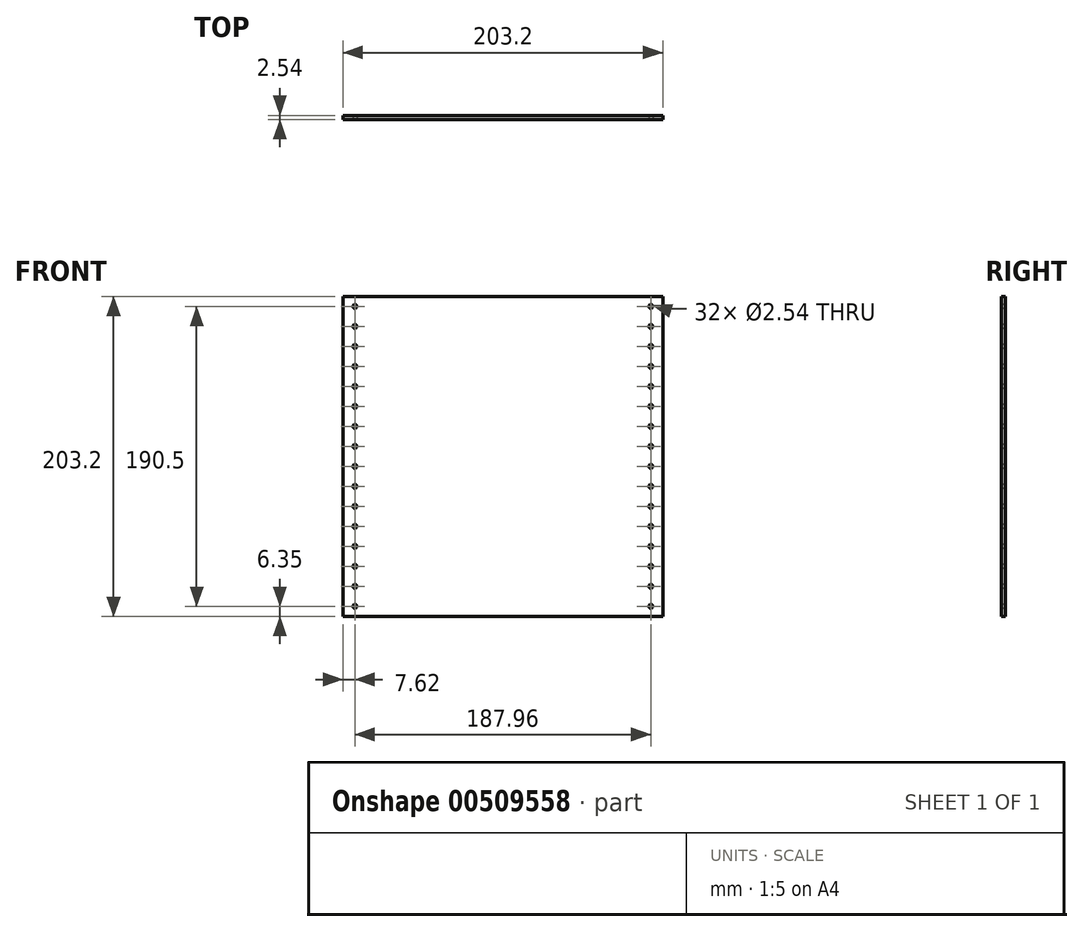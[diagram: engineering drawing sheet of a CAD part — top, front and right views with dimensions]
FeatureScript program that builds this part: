
annotation { "Feature Type Name" : "Feature", "Feature Type Description" : "" }
export const myFeature = defineFeature(function(context is Context, id is Id, definition is map)
    precondition{}
    {
        {
            var Q0;
            Q0=qCreatedBy(makeId("Front.planeOp"),FACE);
            var sketch = newSketch(context, id + "F0", { "sketchPlane" : qUnion([Q0])});
            skLineSegment(sketch, "E0.bottom", {"start": v(0, 0) * mm, "end": v(-203.2, 0) * mm});
            skLineSegment(sketch, "E0.top", {"start": v(0, 203.2) * mm, "end": v(-203.2, 203.2) * mm});
            skLineSegment(sketch, "E0.left", {"start": v(0, 0) * mm, "end": v(0, 203.2) * mm});
            skLineSegment(sketch, "E0.right", {"start": v(-203.2, 0) * mm, "end": v(-203.2, 203.2) * mm});
            skSolve(sketch);
        }
        {
            var Q0;
            Q0=makeQuery(id+"F0.imprint","IMPRINT",FACE,{"disambiguationData":[TD([[makeQuery(id+"F0.imprint","IMPRINT",EDGE,{"derivedFrom":sQuery(id+"F0.wireOp",EDGE,"E0.bottom")}),-1.0]])]});
            extrude(context, id + "F1", {"entities" : qUnion([Q0]), "depth" : 2.54 * mm});
        }
        {
            var Q0;
            Q0=makeQuery(id+"F1.opExtrude","CAP_FACE",FACE,{"disambiguationData":[OSD([sQuery(id+"F0.wireOp",EDGE,"E0.bottom"),sQuery(id+"F0.wireOp",EDGE,"E0.top"),sQuery(id+"F0.wireOp",EDGE,"E0.left"),sQuery(id+"F0.wireOp",EDGE,"E0.right")])],"isStart":false});
            var sketch = newSketch(context, id + "F2", { "sketchPlane" : qUnion([Q0])});
            skLineSegment(sketch, "E1", {"start": v(-203.2, 0) * mm, "end": v(-195.58, 0) * mm});
            skLineSegment(sketch, "E2", {"start": v(-195.58, 0) * mm, "end": v(-195.58, 6.35) * mm});
            skCircle(sketch, "E3", {"center": v(-195.58, 6.35) * mm, "radius": 1.27 * mm});
            skCircle(sketch, "E4.0.1.0", {"center": v(-195.58, 19.05) * mm, "radius": 1.27 * mm});
            skCircle(sketch, "E4.0.2.0", {"center": v(-195.58, 31.75) * mm, "radius": 1.27 * mm});
            skCircle(sketch, "E4.0.3.0", {"center": v(-195.58, 44.45) * mm, "radius": 1.27 * mm});
            skCircle(sketch, "E4.0.4.0", {"center": v(-195.58, 57.15) * mm, "radius": 1.27 * mm});
            skCircle(sketch, "E4.0.5.0", {"center": v(-195.58, 69.85) * mm, "radius": 1.27 * mm});
            skCircle(sketch, "E4.0.6.0", {"center": v(-195.58, 82.55) * mm, "radius": 1.27 * mm});
            skCircle(sketch, "E4.0.7.0", {"center": v(-195.58, 95.25) * mm, "radius": 1.27 * mm});
            skCircle(sketch, "E4.0.8.0", {"center": v(-195.58, 107.95) * mm, "radius": 1.27 * mm});
            skCircle(sketch, "E4.0.9.0", {"center": v(-195.58, 120.65) * mm, "radius": 1.27 * mm});
            skCircle(sketch, "E4.0.10.0", {"center": v(-195.58, 133.35) * mm, "radius": 1.27 * mm});
            skCircle(sketch, "E4.0.11.0", {"center": v(-195.58, 146.05) * mm, "radius": 1.27 * mm});
            skCircle(sketch, "E4.0.12.0", {"center": v(-195.58, 158.75) * mm, "radius": 1.27 * mm});
            skCircle(sketch, "E4.0.13.0", {"center": v(-195.58, 171.45) * mm, "radius": 1.27 * mm});
            skCircle(sketch, "E4.0.14.0", {"center": v(-195.58, 184.15) * mm, "radius": 1.27 * mm});
            skCircle(sketch, "E4.0.15.0", {"center": v(-195.58, 196.85) * mm, "radius": 1.27 * mm});
            skLineSegment(sketch, "E4.direction1", {"start": v(-195.58, 6.35) * mm, "end": v(-170.18, 6.35) * mm, "construction": true});
            skLineSegment(sketch, "E4.direction2", {"start": v(-195.58, 6.35) * mm, "end": v(-195.58, 19.05) * mm, "construction": true});
            skSolve(sketch);
        }
        {
            var Q0;
            Q0=makeQuery(id+"F2.imprint","IMPRINT",FACE,{"disambiguationData":[TD([[makeQuery(id+"F2.imprint","IMPRINT",EDGE,{"derivedFrom":sQuery(id+"F2.wireOp",EDGE,"E4.0.2.0")}),1.0]])]});
            var Q1;
            Q1=makeQuery(id+"F2.imprint","IMPRINT",FACE,{"disambiguationData":[TD([[makeQuery(id+"F2.imprint","IMPRINT",EDGE,{"derivedFrom":sQuery(id+"F2.wireOp",EDGE,"E4.0.3.0")}),1.0]])]});
            var Q2;
            Q2=makeQuery(id+"F2.imprint","IMPRINT",FACE,{"disambiguationData":[TD([[makeQuery(id+"F2.imprint","IMPRINT",EDGE,{"derivedFrom":sQuery(id+"F2.wireOp",EDGE,"E4.0.4.0")}),1.0]])]});
            var Q3;
            Q3=makeQuery(id+"F2.imprint","IMPRINT",FACE,{"disambiguationData":[TD([[makeQuery(id+"F2.imprint","IMPRINT",EDGE,{"derivedFrom":sQuery(id+"F2.wireOp",EDGE,"E4.0.5.0")}),1.0]])]});
            var Q4;
            Q4=makeQuery(id+"F2.imprint","IMPRINT",FACE,{"disambiguationData":[TD([[makeQuery(id+"F2.imprint","IMPRINT",EDGE,{"derivedFrom":sQuery(id+"F2.wireOp",EDGE,"E4.0.6.0")}),1.0]])]});
            var Q5;
            Q5=makeQuery(id+"F2.imprint","IMPRINT",FACE,{"disambiguationData":[TD([[makeQuery(id+"F2.imprint","IMPRINT",EDGE,{"derivedFrom":sQuery(id+"F2.wireOp",EDGE,"E4.0.7.0")}),1.0]])]});
            var Q6;
            Q6=makeQuery(id+"F2.imprint","IMPRINT",FACE,{"disambiguationData":[TD([[makeQuery(id+"F2.imprint","IMPRINT",EDGE,{"derivedFrom":sQuery(id+"F2.wireOp",EDGE,"E4.0.8.0")}),1.0]])]});
            var Q7;
            Q7=makeQuery(id+"F2.imprint","IMPRINT",FACE,{"disambiguationData":[TD([[makeQuery(id+"F2.imprint","IMPRINT",EDGE,{"derivedFrom":sQuery(id+"F2.wireOp",EDGE,"E4.0.9.0")}),1.0]])]});
            var Q8;
            Q8=makeQuery(id+"F2.imprint","IMPRINT",FACE,{"disambiguationData":[TD([[makeQuery(id+"F2.imprint","IMPRINT",EDGE,{"derivedFrom":sQuery(id+"F2.wireOp",EDGE,"E4.0.10.0")}),1.0]])]});
            var Q9;
            Q9=makeQuery(id+"F2.imprint","IMPRINT",FACE,{"disambiguationData":[TD([[makeQuery(id+"F2.imprint","IMPRINT",EDGE,{"derivedFrom":sQuery(id+"F2.wireOp",EDGE,"E4.0.11.0")}),1.0]])]});
            var Q10;
            Q10=makeQuery(id+"F2.imprint","IMPRINT",FACE,{"disambiguationData":[TD([[makeQuery(id+"F2.imprint","IMPRINT",EDGE,{"derivedFrom":sQuery(id+"F2.wireOp",EDGE,"E4.0.12.0")}),1.0]])]});
            var Q11;
            Q11=makeQuery(id+"F2.imprint","IMPRINT",FACE,{"disambiguationData":[TD([[makeQuery(id+"F2.imprint","IMPRINT",EDGE,{"derivedFrom":sQuery(id+"F2.wireOp",EDGE,"E4.0.15.0")}),1.0]])]});
            var Q12;
            Q12=makeQuery(id+"F2.imprint","IMPRINT",FACE,{"disambiguationData":[TD([[makeQuery(id+"F2.imprint","IMPRINT",EDGE,{"derivedFrom":sQuery(id+"F2.wireOp",EDGE,"E4.0.13.0")}),1.0]])]});
            var Q13;
            Q13=makeQuery(id+"F2.imprint","IMPRINT",FACE,{"disambiguationData":[TD([[makeQuery(id+"F2.imprint","IMPRINT",EDGE,{"derivedFrom":sQuery(id+"F2.wireOp",EDGE,"E4.0.14.0")}),1.0]])]});
            var Q14;
            Q14=makeQuery(id+"F2.imprint","IMPRINT",FACE,{"disambiguationData":[TD([[makeQuery(id+"F2.imprint","IMPRINT",EDGE,{"derivedFrom":sQuery(id+"F2.wireOp",EDGE,"E4.0.1.0")}),1.0]])]});
            var Q15;
            Q15=makeQuery(id+"F2.imprint","IMPRINT",FACE,{"disambiguationData":[TD([[makeQuery(id+"F2.imprint","IMPRINT",EDGE,{"derivedFrom":sQuery(id+"F2.wireOp",EDGE,"E3")}),1.0]])]});
            extrude(context, id + "F3", {"entities" : qUnion([Q0, Q1, Q2, Q3, Q4, Q5, Q6, Q7, Q8, Q9, Q10, Q11, Q12, Q13, Q14, Q15]), "operationType" : NewBodyOperationType.REMOVE, "oppositeDirection" : true, "depth" : 25.4 * mm});
        }
        {
            var Q0;
            Q0=makeQuery(id+"F1.opExtrude","CAP_FACE",FACE,{"disambiguationData":[OSD([sQuery(id+"F0.wireOp",EDGE,"E0.bottom"),sQuery(id+"F0.wireOp",EDGE,"E0.top"),sQuery(id+"F0.wireOp",EDGE,"E0.left"),sQuery(id+"F0.wireOp",EDGE,"E0.right")])],"isStart":false});
            var sketch = newSketch(context, id + "F4", { "sketchPlane" : qUnion([Q0])});
            skLineSegment(sketch, "E5", {"start": v(0, 0) * mm, "end": v(-7.62, 0) * mm});
            skLineSegment(sketch, "E6", {"start": v(-7.62, 0) * mm, "end": v(-7.62, 6.35) * mm});
            skCircle(sketch, "E7", {"center": v(-7.62, 6.35) * mm, "radius": 1.27 * mm});
            skCircle(sketch, "E8.0.1.0", {"center": v(-7.62, 19.05) * mm, "radius": 1.27 * mm});
            skCircle(sketch, "E8.0.2.0", {"center": v(-7.62, 31.75) * mm, "radius": 1.27 * mm});
            skCircle(sketch, "E8.0.3.0", {"center": v(-7.62, 44.45) * mm, "radius": 1.27 * mm});
            skCircle(sketch, "E8.0.4.0", {"center": v(-7.62, 57.15) * mm, "radius": 1.27 * mm});
            skCircle(sketch, "E8.0.5.0", {"center": v(-7.62, 69.85) * mm, "radius": 1.27 * mm});
            skCircle(sketch, "E8.0.6.0", {"center": v(-7.62, 82.55) * mm, "radius": 1.27 * mm});
            skCircle(sketch, "E8.0.7.0", {"center": v(-7.62, 95.25) * mm, "radius": 1.27 * mm});
            skCircle(sketch, "E8.0.8.0", {"center": v(-7.62, 107.95) * mm, "radius": 1.27 * mm});
            skCircle(sketch, "E8.0.9.0", {"center": v(-7.62, 120.65) * mm, "radius": 1.27 * mm});
            skCircle(sketch, "E8.0.10.0", {"center": v(-7.62, 133.35) * mm, "radius": 1.27 * mm});
            skCircle(sketch, "E8.0.11.0", {"center": v(-7.62, 146.05) * mm, "radius": 1.27 * mm});
            skCircle(sketch, "E8.0.12.0", {"center": v(-7.62, 158.75) * mm, "radius": 1.27 * mm});
            skCircle(sketch, "E8.0.13.0", {"center": v(-7.62, 171.45) * mm, "radius": 1.27 * mm});
            skCircle(sketch, "E8.0.14.0", {"center": v(-7.62, 184.15) * mm, "radius": 1.27 * mm});
            skCircle(sketch, "E8.0.15.0", {"center": v(-7.62, 196.85) * mm, "radius": 1.27 * mm});
            skLineSegment(sketch, "E8.direction1", {"start": v(-7.62, 6.35) * mm, "end": v(17.78, 6.35) * mm, "construction": true});
            skLineSegment(sketch, "E8.direction2", {"start": v(-7.62, 6.35) * mm, "end": v(-7.62, 19.05) * mm, "construction": true});
            skSolve(sketch);
        }
        {
            var Q0;
            Q0=makeQuery(id+"F4.imprint","IMPRINT",FACE,{"disambiguationData":[TD([[makeQuery(id+"F4.imprint","IMPRINT",EDGE,{"derivedFrom":sQuery(id+"F4.wireOp",EDGE,"E8.0.3.0")}),1.0]])]});
            var Q1;
            Q1=makeQuery(id+"F4.imprint","IMPRINT",FACE,{"disambiguationData":[TD([[makeQuery(id+"F4.imprint","IMPRINT",EDGE,{"derivedFrom":sQuery(id+"F4.wireOp",EDGE,"E8.0.4.0")}),1.0]])]});
            var Q2;
            Q2=makeQuery(id+"F4.imprint","IMPRINT",FACE,{"disambiguationData":[TD([[makeQuery(id+"F4.imprint","IMPRINT",EDGE,{"derivedFrom":sQuery(id+"F4.wireOp",EDGE,"E8.0.5.0")}),1.0]])]});
            var Q3;
            Q3=makeQuery(id+"F4.imprint","IMPRINT",FACE,{"disambiguationData":[TD([[makeQuery(id+"F4.imprint","IMPRINT",EDGE,{"derivedFrom":sQuery(id+"F4.wireOp",EDGE,"E8.0.6.0")}),1.0]])]});
            var Q4;
            Q4=makeQuery(id+"F4.imprint","IMPRINT",FACE,{"disambiguationData":[TD([[makeQuery(id+"F4.imprint","IMPRINT",EDGE,{"derivedFrom":sQuery(id+"F4.wireOp",EDGE,"E8.0.7.0")}),1.0]])]});
            var Q5;
            Q5=makeQuery(id+"F4.imprint","IMPRINT",FACE,{"disambiguationData":[TD([[makeQuery(id+"F4.imprint","IMPRINT",EDGE,{"derivedFrom":sQuery(id+"F4.wireOp",EDGE,"E8.0.8.0")}),1.0]])]});
            var Q6;
            Q6=makeQuery(id+"F4.imprint","IMPRINT",FACE,{"disambiguationData":[TD([[makeQuery(id+"F4.imprint","IMPRINT",EDGE,{"derivedFrom":sQuery(id+"F4.wireOp",EDGE,"E8.0.9.0")}),1.0]])]});
            var Q7;
            Q7=makeQuery(id+"F4.imprint","IMPRINT",FACE,{"disambiguationData":[TD([[makeQuery(id+"F4.imprint","IMPRINT",EDGE,{"derivedFrom":sQuery(id+"F4.wireOp",EDGE,"E8.0.10.0")}),1.0]])]});
            var Q8;
            Q8=makeQuery(id+"F4.imprint","IMPRINT",FACE,{"disambiguationData":[TD([[makeQuery(id+"F4.imprint","IMPRINT",EDGE,{"derivedFrom":sQuery(id+"F4.wireOp",EDGE,"E8.0.15.0")}),1.0]])]});
            var Q9;
            Q9=makeQuery(id+"F4.imprint","IMPRINT",FACE,{"disambiguationData":[TD([[makeQuery(id+"F4.imprint","IMPRINT",EDGE,{"derivedFrom":sQuery(id+"F4.wireOp",EDGE,"E8.0.13.0")}),1.0]])]});
            var Q10;
            Q10=makeQuery(id+"F4.imprint","IMPRINT",FACE,{"disambiguationData":[TD([[makeQuery(id+"F4.imprint","IMPRINT",EDGE,{"derivedFrom":sQuery(id+"F4.wireOp",EDGE,"E8.0.14.0")}),1.0]])]});
            var Q11;
            Q11=makeQuery(id+"F4.imprint","IMPRINT",FACE,{"disambiguationData":[TD([[makeQuery(id+"F4.imprint","IMPRINT",EDGE,{"derivedFrom":sQuery(id+"F4.wireOp",EDGE,"E8.0.2.0")}),1.0]])]});
            var Q12;
            Q12=makeQuery(id+"F4.imprint","IMPRINT",FACE,{"disambiguationData":[TD([[makeQuery(id+"F4.imprint","IMPRINT",EDGE,{"derivedFrom":sQuery(id+"F4.wireOp",EDGE,"E8.0.11.0")}),1.0]])]});
            var Q13;
            Q13=makeQuery(id+"F4.imprint","IMPRINT",FACE,{"disambiguationData":[TD([[makeQuery(id+"F4.imprint","IMPRINT",EDGE,{"derivedFrom":sQuery(id+"F4.wireOp",EDGE,"E8.0.12.0")}),1.0]])]});
            var Q14;
            Q14=makeQuery(id+"F4.imprint","IMPRINT",FACE,{"disambiguationData":[TD([[makeQuery(id+"F4.imprint","IMPRINT",EDGE,{"derivedFrom":sQuery(id+"F4.wireOp",EDGE,"E8.0.1.0")}),1.0]])]});
            var Q15;
            Q15=makeQuery(id+"F4.imprint","IMPRINT",FACE,{"disambiguationData":[TD([[makeQuery(id+"F4.imprint","IMPRINT",EDGE,{"derivedFrom":sQuery(id+"F4.wireOp",EDGE,"E7")}),1.0]])]});
            extrude(context, id + "F5", {"entities" : qUnion([Q0, Q1, Q2, Q3, Q4, Q5, Q6, Q7, Q8, Q9, Q10, Q11, Q12, Q13, Q14, Q15]), "operationType" : NewBodyOperationType.REMOVE, "oppositeDirection" : true, "depth" : 25.4 * mm});
        }
    });
